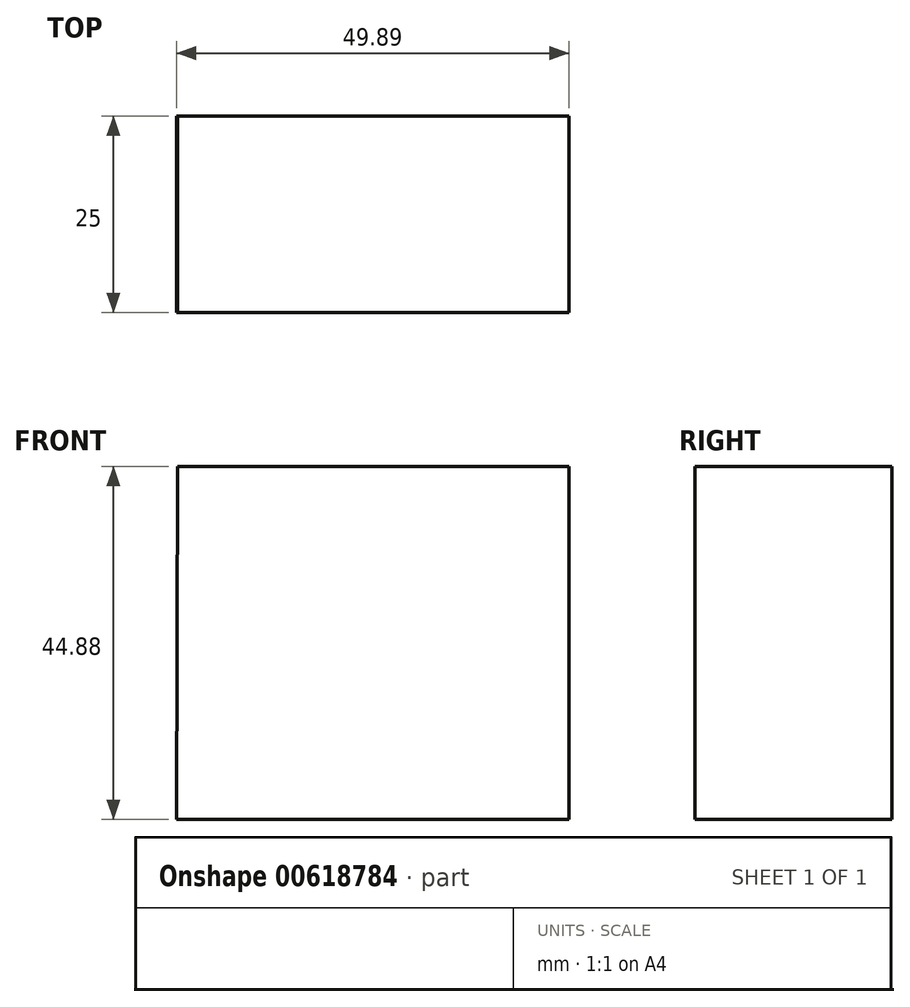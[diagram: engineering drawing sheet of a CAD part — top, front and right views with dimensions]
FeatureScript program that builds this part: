
annotation { "Feature Type Name" : "Feature", "Feature Type Description" : "" }
export const myFeature = defineFeature(function(context is Context, id is Id, definition is map)
    precondition{}
    {
        {
            var Q0;
            Q0=qCreatedBy(makeId("Front.planeOp"),FACE);
            var sketch = newSketch(context, id + "F0", { "sketchPlane" : qUnion([Q0])});
            skLineSegment(sketch, "E0", {"start": v(-49.75, 56.69) * mm, "end": v(0, 56.69) * mm});
            skLineSegment(sketch, "E1", {"start": v(0, 56.69) * mm, "end": v(0, 11.8) * mm});
            skLineSegment(sketch, "E2", {"start": v(0, 11.8) * mm, "end": v(-49.9, 11.8) * mm});
            skLineSegment(sketch, "E3", {"start": v(-49.9, 11.8) * mm, "end": v(-49.75, 56.69) * mm});
            skSolve(sketch);
        }
        {
            var Q0;
            Q0=makeQuery(id+"F0.imprint","IMPRINT",FACE,{"disambiguationData":[TD([[makeQuery(id+"F0.imprint","IMPRINT",EDGE,{"derivedFrom":sQuery(id+"F0.wireOp",EDGE,"E0")}),-1.0]])]});
            extrude(context, id + "F1", {"entities" : qUnion([Q0]), "depth" : 25 * mm, "offsetDistance" : 25 * mm});
        }
    });
